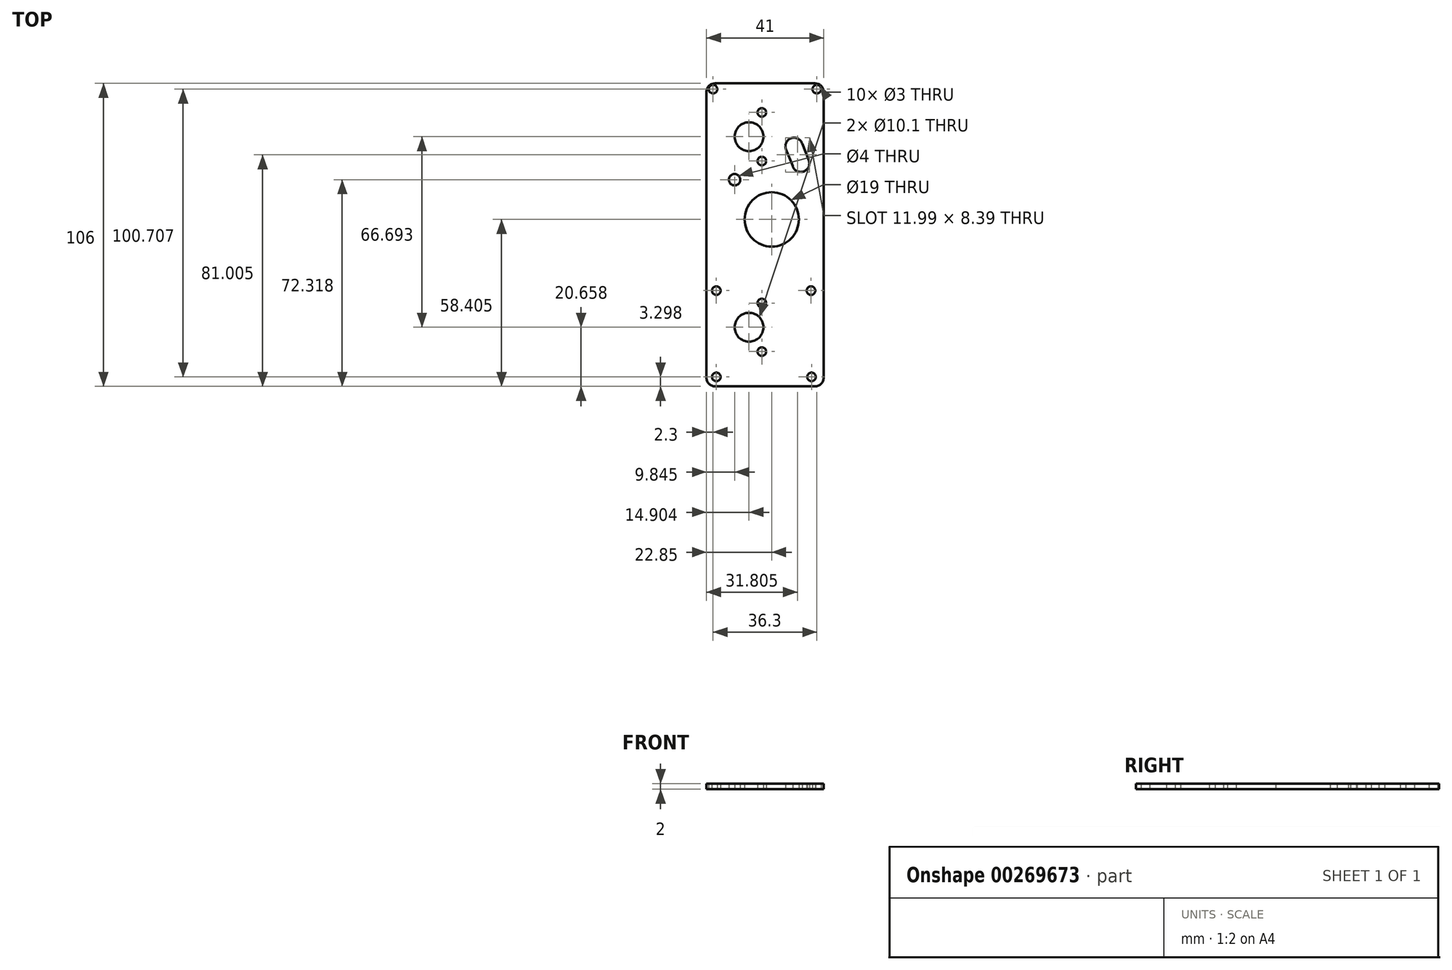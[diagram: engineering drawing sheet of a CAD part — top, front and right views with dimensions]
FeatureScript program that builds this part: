
annotation { "Feature Type Name" : "Feature", "Feature Type Description" : "" }
export const myFeature = defineFeature(function(context is Context, id is Id, definition is map)
    precondition{}
    {
        {
            var Q0;
            Q0=qCreatedBy(makeId("Top.planeOp"),FACE);
            var sketch = newSketch(context, id + "F0", { "sketchPlane" : qUnion([Q0])});
            skCircle(sketch, "E0", {"center": v(-18.23, -50.84) * mm, "radius": 1.5 * mm});
            skCircle(sketch, "E1", {"center": v(-18.23, -20.64) * mm, "radius": 1.5 * mm});
            skCircle(sketch, "E2", {"center": v(16.92, 49.86) * mm, "radius": 1.5 * mm});
            skCircle(sketch, "E3", {"center": v(-19.38, 49.86) * mm, "radius": 1.5 * mm});
            skLineSegment(sketch, "E4.bottom", {"start": v(-21.68, 51.86) * mm, "end": v(19.32, 51.86) * mm});
            skLineSegment(sketch, "E4.top", {"start": v(-21.68, -54.14) * mm, "end": v(19.32, -54.14) * mm});
            skLineSegment(sketch, "E4.left", {"start": v(-21.68, 51.86) * mm, "end": v(-21.68, -54.14) * mm});
            skLineSegment(sketch, "E4.right", {"start": v(19.32, 51.86) * mm, "end": v(19.32, -54.14) * mm});
            skArc(sketch, "E5", {"start": v(-8.05, 46.53) * mm, "mid": v(-4.94, 40.84) * mm, "end": v(1, 38.21) * mm});
            skLineSegment(sketch, "E6", {"start": v(1, 38.21) * mm, "end": v(1, 28.21) * mm});
            skLineSegment(sketch, "E7", {"start": v(-11.86, 33.21) * mm, "end": v(22.45, 33.21) * mm, "construction": true});
            skArc(sketch, "E8.MirrorCS", {"start": v(-8.05, 19.89) * mm, "mid": v(-4.94, 25.58) * mm, "end": v(1, 28.21) * mm});
            skCircle(sketch, "E9", {"center": v(-2.3, 41.71) * mm, "radius": 1.5 * mm});
            skCircle(sketch, "E10.MirrorC", {"center": v(-2.3, 24.71) * mm, "radius": 1.5 * mm});
            skCircle(sketch, "E11", {"center": v(-6.78, 33.21) * mm, "radius": 5.05 * mm});
            skLineSegment(sketch, "E12", {"start": v(-28.15, -0.14) * mm, "end": v(20.86, -0.14) * mm, "construction": true});
            skCircle(sketch, "E13.MirrorC", {"center": v(-2.3, -24.98) * mm, "radius": 1.5 * mm});
            skArc(sketch, "E14.MirrorCS", {"start": v(-8.05, -20.16) * mm, "mid": v(-4.94, -25.86) * mm, "end": v(1, -28.48) * mm});
            skLineSegment(sketch, "E15.MirrorCS", {"start": v(1, -38.48) * mm, "end": v(1, -28.48) * mm});
            skArc(sketch, "E16.MirrorCS", {"start": v(-8.05, -46.8) * mm, "mid": v(-4.94, -41.1) * mm, "end": v(1, -38.48) * mm});
            skCircle(sketch, "E17.MirrorC", {"center": v(-2.3, -41.98) * mm, "radius": 1.5 * mm});
            skCircle(sketch, "E18.MirrorC", {"center": v(-6.78, -33.48) * mm, "radius": 5.05 * mm});
            skLineSegment(sketch, "E19", {"start": v(-4.93, -17.22) * mm, "end": v(-4.93, -48.35) * mm, "construction": true});
            skLineSegment(sketch, "E20", {"start": v(10, -20.52) * mm, "end": v(10, -46.52) * mm});
            skLineSegment(sketch, "E21", {"start": v(10, -46.52) * mm, "end": v(-8.05, -46.8) * mm});
            skLineSegment(sketch, "E22", {"start": v(10, -20.52) * mm, "end": v(-8.05, -20.16) * mm});
            skLineSegment(sketch, "E23.MirrorCS", {"start": v(10, 20.25) * mm, "end": v(-8.05, 19.89) * mm});
            skLineSegment(sketch, "E24.MirrorCS", {"start": v(10, 20.25) * mm, "end": v(10, 46.25) * mm});
            skLineSegment(sketch, "E25.MirrorCS", {"start": v(10, 46.25) * mm, "end": v(-8.05, 46.53) * mm});
            skCircle(sketch, "E26", {"center": v(1.17, 4.26) * mm, "radius": 9.5 * mm});
            skCircle(sketch, "E27", {"center": v(11.32, 23.86) * mm, "radius": 3 * mm});
            skCircle(sketch, "E28", {"center": v(-11.84, -0.14) * mm, "radius": 2 * mm});
            skCircle(sketch, "E29", {"center": v(-11.84, -18.45) * mm, "radius": 2 * mm});
            skCircle(sketch, "E30.MirrorC", {"center": v(-11.84, 18.18) * mm, "radius": 2 * mm});
            skCircle(sketch, "E31", {"center": v(8.93, 29.86) * mm, "radius": 3 * mm});
            skLineSegment(sketch, "E32", {"start": v(11.77, 30.82) * mm, "end": v(14.1, 24.98) * mm});
            skLineSegment(sketch, "E33", {"start": v(8.61, 22.57) * mm, "end": v(6.14, 28.75) * mm});
            skCircle(sketch, "E34", {"center": v(14.89, -20.64) * mm, "radius": 1.5 * mm});
            skCircle(sketch, "E35", {"center": v(15.07, -50.84) * mm, "radius": 1.5 * mm});
            skSolve(sketch);
        }
        {
            var Q0;
            Q0=makeQuery(id+"F0.imprint","IMPRINT",FACE,{"disambiguationData":[TD([[makeQuery(id+"F0.imprint","IMPRINT",EDGE,{"derivedFrom":sQuery(id+"F0.wireOp",EDGE,"5e25448f-ad87-4180-8a74-d3dedaf74bf8")}),-1.0]])]});
            var Q1;
            Q1=makeQuery(id+"F0.imprint","IMPRINT",FACE,{"disambiguationData":[TD([[makeQuery(id+"F0.imprint","IMPRINT",EDGE,{"derivedFrom":sQuery(id+"F0.wireOp",EDGE,"E5")}),1.0]])]});
            var Q2;
            Q2=makeQuery(id+"F0.imprint","IMPRINT",FACE,{"disambiguationData":[TD([[makeQuery(id+"F0.imprint","IMPRINT",EDGE,{"derivedFrom":sQuery(id+"F0.wireOp",EDGE,"E29")}),1.0]])]});
            var Q3;
            Q3=makeQuery(id+"F0.imprint","IMPRINT",FACE,{"disambiguationData":[TD([[makeQuery(id+"F0.imprint","IMPRINT",EDGE,{"derivedFrom":sQuery(id+"F0.wireOp",EDGE,"E13.MirrorC")}),-1.0]])]});
            var Q4;
            Q4=makeQuery(id+"F0.imprint","IMPRINT",FACE,{"disambiguationData":[TD([[makeQuery(id+"F0.imprint","IMPRINT",EDGE,{"derivedFrom":sQuery(id+"F0.wireOp",EDGE,"E28")}),1.0]])]});
            var Q5;
            Q5=makeQuery(id+"F0.imprint","IMPRINT",FACE,{"disambiguationData":[TD([[makeQuery(id+"F0.imprint","IMPRINT",EDGE,{"derivedFrom":sQuery(id+"F0.wireOp",EDGE,"E30.MirrorC")}),-1.0]])]});
            var Q6;
            Q6=makeQuery(id+"F0.imprint","IMPRINT",FACE,{"disambiguationData":[TD([[makeQuery(id+"F0.imprint","IMPRINT",EDGE,{"derivedFrom":sQuery(id+"F0.wireOp",EDGE,"E0")}),-1.0]])]});
            extrude(context, id + "F1", {"entities" : qUnion([Q0, Q1, Q2, Q3, Q4, Q5, Q6]), "depth" : 2 * mm});
        }
        {
            var Q0;
            Q0=makeQuery(id+"F1.opExtrude","SWEPT_EDGE",EDGE,{"disambiguationData":[OSD([sQuery(id+"F0.wireOp",EDGE,"E4.bottom"),sQuery(id+"F0.wireOp",EDGE,"E4.left")])]});
            var Q1;
            Q1=makeQuery(id+"F1.opExtrude","SWEPT_EDGE",EDGE,{"disambiguationData":[OSD([sQuery(id+"F0.wireOp",EDGE,"E4.top"),sQuery(id+"F0.wireOp",EDGE,"E4.left")])]});
            var Q2;
            Q2=makeQuery(id+"F1.opExtrude","SWEPT_EDGE",EDGE,{"disambiguationData":[OSD([sQuery(id+"F0.wireOp",EDGE,"E4.top"),sQuery(id+"F0.wireOp",EDGE,"E4.right")])]});
            var Q3;
            Q3=makeQuery(id+"F1.opExtrude","SWEPT_EDGE",EDGE,{"disambiguationData":[OSD([sQuery(id+"F0.wireOp",EDGE,"E4.bottom"),sQuery(id+"F0.wireOp",EDGE,"E4.right")])]});
            fillet(context, id + "F2", {"entities" : qUnion([Q0, Q1, Q2, Q3]), "radius" : 3 * mm, "tangentPropagation" : true, "allowEdgeOverflow" : false});
        }
    });
